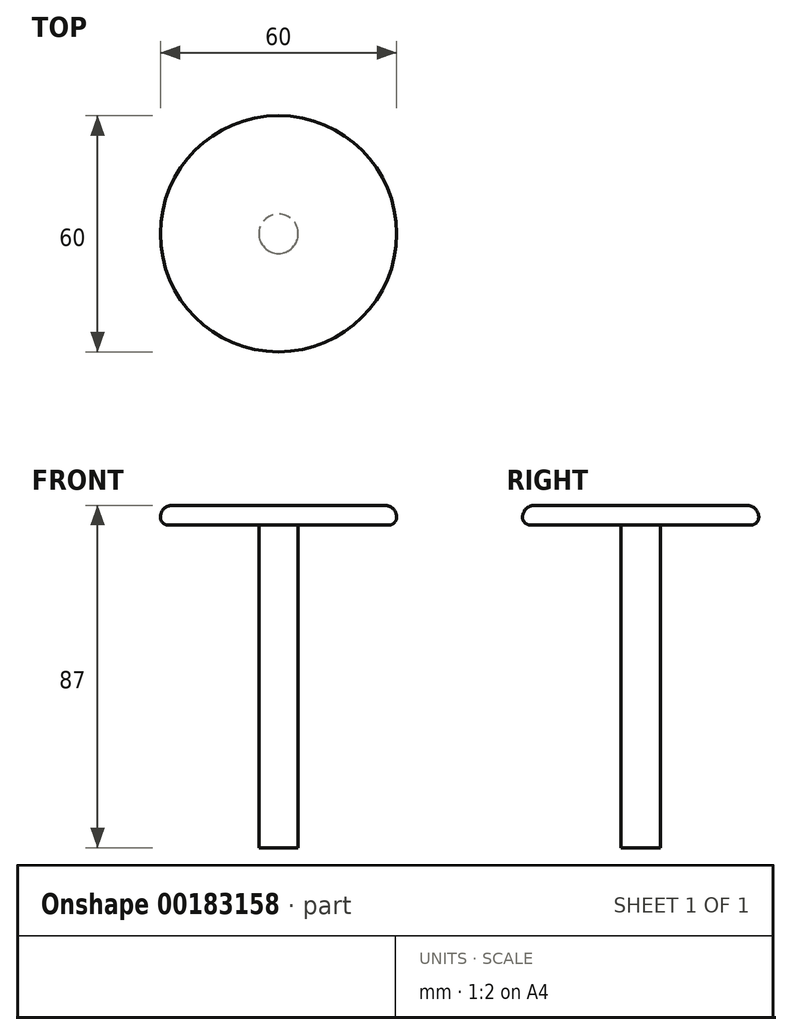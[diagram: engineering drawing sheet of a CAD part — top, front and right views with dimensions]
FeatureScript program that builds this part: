
annotation { "Feature Type Name" : "Feature", "Feature Type Description" : "" }
export const myFeature = defineFeature(function(context is Context, id is Id, definition is map)
    precondition{}
    {
        {
            var Q0;
            Q0=qCreatedBy(makeId("Top.planeOp"),FACE);
            var sketch = newSketch(context, id + "F0", { "sketchPlane" : qUnion([Q0])});
            skCircle(sketch, "E0", {"center": v(0, 0) * mm, "radius": 30 * mm});
            skSolve(sketch);
        }
        {
            var Q0;
            Q0 = qSketchRegion(id + "F0", true);
            extrude(context, id + "F1", {"entities" : qUnion([Q0]), "depth" : 5 * mm});
        }
        {
            var Q0;
            Q0=makeQuery(id+"F1.opExtrude","CAP_EDGE",EDGE,{"disambiguationData":[OSD([sQuery(id+"F0.wireOp",EDGE,"E0")])],"isStart":false});
            fillet(context, id + "F2", {"entities" : qUnion([Q0]), "radius" : 3 * mm, "tangentPropagation" : true, "allowEdgeOverflow" : false});
        }
        {
            var Q0;
            Q0=makeQuery(id+"F1.opExtrude","CAP_EDGE",EDGE,{"disambiguationData":[OSD([sQuery(id+"F0.wireOp",EDGE,"E0")])],"isStart":true});
            fillet(context, id + "F3", {"entities" : qUnion([Q0]), "radius" : 2 * mm, "tangentPropagation" : true, "allowEdgeOverflow" : false});
        }
        {
            var Q0;
            Q0=makeQuery(id+"F1.opExtrude","CAP_FACE",FACE,{"disambiguationData":[OSD([sQuery(id+"F0.wireOp",EDGE,"E0")])],"isStart":true});
            var sketch = newSketch(context, id + "F4", { "sketchPlane" : qUnion([Q0])});
            skCircle(sketch, "E1", {"center": v(0, 0) * mm, "radius": 5 * mm});
            skSolve(sketch);
        }
        {
            var Q0;
            Q0 = qSketchRegion(id + "F4", true);
            extrude(context, id + "F5", {"entities" : qUnion([Q0]), "operationType" : NewBodyOperationType.ADD, "depth" : 82 * mm});
        }
    });
